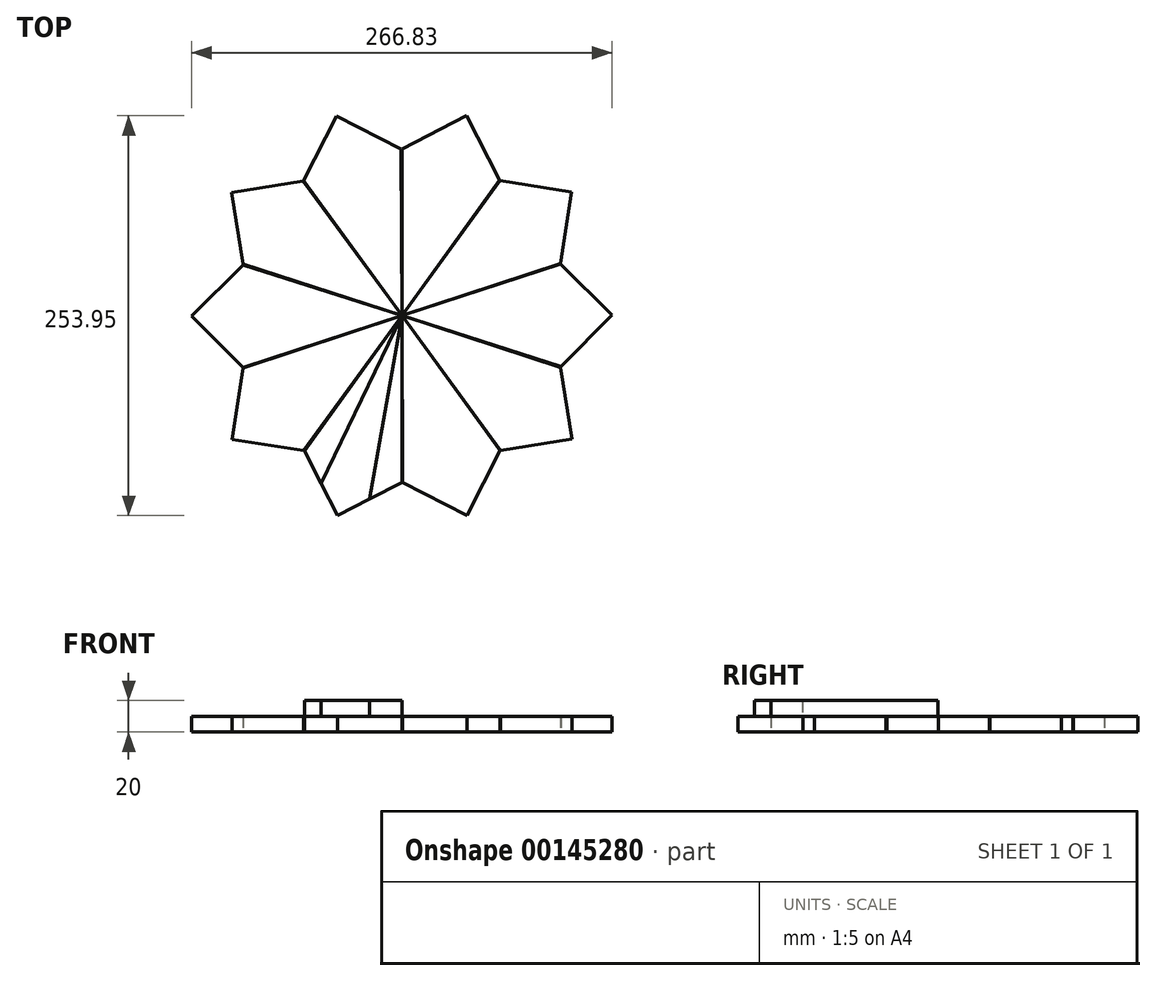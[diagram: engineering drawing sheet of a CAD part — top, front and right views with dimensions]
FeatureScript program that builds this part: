
annotation { "Feature Type Name" : "Feature", "Feature Type Description" : "" }
export const myFeature = defineFeature(function(context is Context, id is Id, definition is map)
    precondition{}
    {
        {
            var Q0;
            Q0=qCreatedBy(makeId("Top.planeOp"),FACE);
            var sketch = newSketch(context, id + "F0", { "sketchPlane" : qUnion([Q0])});
            skLineSegment(sketch, "E0.bottom", {"start": v(-76.85, 63.45) * mm, "end": v(73.15, 63.45) * mm});
            skLineSegment(sketch, "E0.top", {"start": v(-76.85, -86.55) * mm, "end": v(73.15, -86.55) * mm});
            skLineSegment(sketch, "E0.left", {"start": v(-76.85, 63.45) * mm, "end": v(-76.85, -86.55) * mm});
            skLineSegment(sketch, "E0.right", {"start": v(73.15, 63.45) * mm, "end": v(73.15, -86.55) * mm});
            skLineSegment(sketch, "E1", {"start": v(-76.85, 63.45) * mm, "end": v(73.15, -86.55) * mm});
            skLineSegment(sketch, "E2", {"start": v(73.15, 63.45) * mm, "end": v(-76.85, -86.55) * mm});
            skLineSegment(sketch, "E3", {"start": v(-1.85, 63.45) * mm, "end": v(-1.85, -86.55) * mm});
            skLineSegment(sketch, "E4", {"start": v(-76.85, -11.55) * mm, "end": v(73.15, -11.55) * mm});
            skLineSegment(sketch, "E5", {"start": v(-289.8, 36.57) * mm, "end": v(-289.8, -69.43) * mm});
            skLineSegment(sketch, "E6", {"start": v(-351.72, -49.46) * mm, "end": v(-289.8, 36.57) * mm});
            skLineSegment(sketch, "E7", {"start": v(-351.72, -49.46) * mm, "end": v(-330.74, -90.4) * mm});
            skLineSegment(sketch, "E8", {"start": v(-330.74, -90.4) * mm, "end": v(-289.8, -69.43) * mm});
            skLineSegment(sketch, "E9", {"start": v(-289.8, 36.57) * mm, "end": v(-343.77, -64.98) * mm});
            skLineSegment(sketch, "E10", {"start": v(-289.8, 36.57) * mm, "end": v(-305.32, -77.37) * mm});
            skSolve(sketch);
        }
        {
            var Q0;
            {var subQ3=sQuery(id+"F0.wireOp",EDGE,"E9");Q0=makeQuery(id+"F0.imprint","IMPRINT",FACE,{"disambiguationData":[TD([[makeQuery(id+"F0.imprint","IMPRINT",EDGE,{"derivedFrom":subQ3}),1.0]])]});}
            var Q1;
            {var subQ0=sQuery(id+"F0.wireOp",EDGE,"E6");Q1=makeQuery(id+"F0.imprint","IMPRINT",FACE,{"disambiguationData":[TD([[makeQuery(id+"F0.imprint","IMPRINT",EDGE,{"derivedFrom":subQ0}),-1.0]])]});}
            var Q2;
            {var subQ0=sQuery(id+"F0.wireOp",EDGE,"E5");Q2=makeQuery(id+"F0.imprint","IMPRINT",FACE,{"disambiguationData":[TD([[makeQuery(id+"F0.imprint","IMPRINT",EDGE,{"derivedFrom":subQ0}),-1.0]])]});}
            extrude(context, id + "F1", {"entities" : qUnion([Q0, Q1, Q2]), "depth" : 10 * mm});
        }
        {
            var Q0;
            Q0=makeQuery(id+"F1.opExtrude","CAP_FACE",FACE,{"disambiguationData":[OSD([sQuery(id+"F0.wireOp",EDGE,"E5"),sQuery(id+"F0.wireOp",EDGE,"E6"),sQuery(id+"F0.wireOp",EDGE,"E7"),sQuery(id+"F0.wireOp",EDGE,"E8")])],"isStart":false});
            var sketch = newSketch(context, id + "F2", { "sketchPlane" : qUnion([Q0])});
            skLineSegment(sketch, "E11", {"start": v(-289.8, 36.57) * mm, "end": v(-341.23, -69.93) * mm});
            skLineSegment(sketch, "E12", {"start": v(-289.8, 36.57) * mm, "end": v(-310.27, -79.91) * mm});
            skLineSegment(sketch, "E13", {"start": v(-310.27, -79.91) * mm, "end": v(-289.8, -69.43) * mm});
            skLineSegment(sketch, "E14", {"start": v(-289.8, -69.43) * mm, "end": v(-289.8, 36.57) * mm});
            skLineSegment(sketch, "E15", {"start": v(-289.8, 36.57) * mm, "end": v(-351.72, -49.46) * mm});
            skLineSegment(sketch, "E16", {"start": v(-351.72, -49.46) * mm, "end": v(-341.23, -69.93) * mm});
            skSolve(sketch);
        }
        {
            var Q0;
            Q0 = qSketchRegion(id + "F2", true);
            extrude(context, id + "F3", {"entities" : qUnion([Q0]), "depth" : 10 * mm});
        }
        {
            var Q0;
            Q0=makeQuery(id+"F1.opExtrude","SWEPT_BODY",BODY,{"disambiguationData":[OSD([sQuery(id+"F0.wireOp",EDGE,"E5"),sQuery(id+"F0.wireOp",EDGE,"E6"),sQuery(id+"F0.wireOp",EDGE,"E7"),sQuery(id+"F0.wireOp",EDGE,"E8")])]});
            var Q1;
            Q1=makeQuery(id+"FQBkqaozaXXL2QT_1.opExtrude","SWEPT_BODY",BODY,{"disambiguationData":[OSD([sQuery(id+"F0.wireOp",EDGE,"E5"),sQuery(id+"F0.wireOp",EDGE,"E8"),sQuery(id+"F0.wireOp",EDGE,"E10")])]});
            var Q2;
            Q2=makeQuery(id+"FQBkqaozaXXL2QT_1.opExtrude","SWEPT_BODY",BODY,{"disambiguationData":[OSD([sQuery(id+"F0.wireOp",EDGE,"E6"),sQuery(id+"F0.wireOp",EDGE,"E7"),sQuery(id+"F0.wireOp",EDGE,"E9")])]});
            var Q3;
            Q3=makeQuery(id+"F1.opExtrude","SWEPT_EDGE",EDGE,{"disambiguationData":[OSD([sQuery(id+"F0.wireOp",EDGE,"E5"),sQuery(id+"F0.wireOp",EDGE,"E6")])]});
            circularPattern(context, id + "F4", {"entities" : qUnion([Q0, Q1, Q2]), "axis" : qUnion([Q3]), "angle" : 360 * degree, "instanceCount" : 10, "equalSpace" : true});
        }
    });
